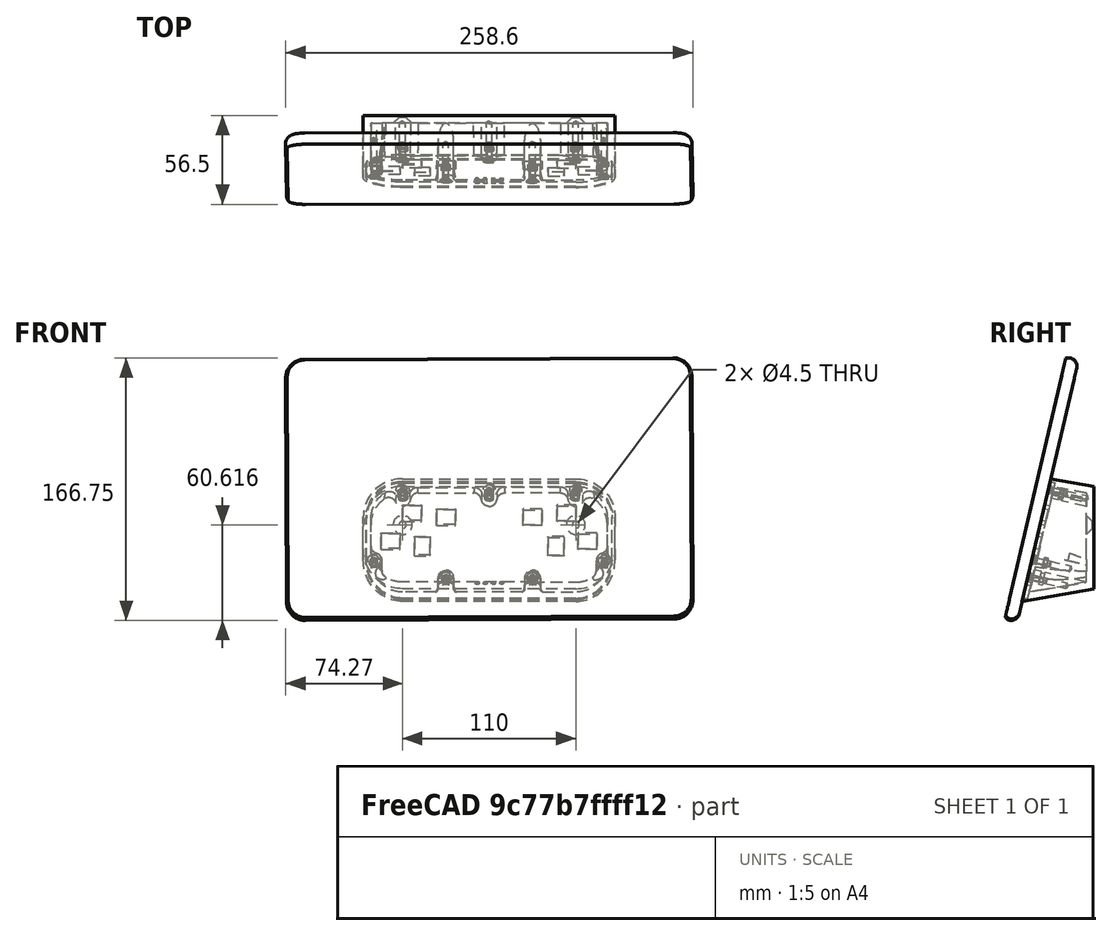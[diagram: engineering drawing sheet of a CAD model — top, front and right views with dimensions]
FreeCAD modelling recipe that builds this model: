
FCSTD DOCUMENT  (FreeCAD 0.21R33668 +7 (Git))
Label: assembly
License: All rights reserved
LicenseURL: http://en.wikipedia.org/wiki/All_rights_reserved
objects: Part::FeaturePython×9, App::GeometryPython×2
note: 9 computed .brp shape members not serialized (recipe doc carries the construction recipe); baked Part::Feature solids carry a one-line shape summary decoded from their .brp

FEATURE [Part::FeaturePython] b_wall_mount_001_  label="wall-mount_001"  # a2plus imported part (geometry in sourceFile) (typed FeaturePython)
  a2p_Version = 0.4.60n
  fixedPosition = true
  objectType = a2pPart
  sourceFile = ./wall-mount.FCStd
  subassemblyImport = false
  timeLastImport = 1.6917e+09
  updateColors = true
FEATURE [Part::FeaturePython] b_pixel_tablet_001_  label="pixel-tablet_001"  # a2plus imported part (geometry in sourceFile) (typed FeaturePython)
  Placement = pos=(0.0336065,-37.299,60.3169) rot=(-0.227279,-0.004053,0.000467;0.229357rad)
  a2p_Version = 0.4.60n
  fixedPosition = false
  objectType = a2pPart
  sourceFile = ./pixel-tablet.FCStd
  subassemblyImport = false
  timeLastImport = 1.69169e+09
  updateColors = true
FEATURE [Part::FeaturePython] Screw  label="M3x12-Screw"  # Fasteners workbench fastener (typed FeaturePython)
  Placement = pos=(-27.5,-42.008,4.07) rot=(1,0,0;1.34148rad)
  baseObject = -> b_wall_mount_001_ [Edge443]
  diameter = 3
  invert = true
  leftHanded = false
  length = 2
  lengthCustom = 12
  matchOuter = false
  offset = 0
  thread = false
  type = 31
FEATURE [Part::FeaturePython] Screw001  label="M3x12-Screw001"  # Fasteners workbench fastener (typed FeaturePython)
  Placement = pos=(27.5,-42.008,4.07) rot=(1,0,0;1.34148rad)
  baseObject = -> b_wall_mount_001_ [Edge451]
  diameter = 3
  invert = false
  leftHanded = false
  length = 2
  lengthCustom = 12
  matchOuter = false
  offset = 0
  thread = false
  type = 31
FEATURE [Part::FeaturePython] Screw002  label="M3x12-Screw002"  # Fasteners workbench fastener (typed FeaturePython)
  Placement = pos=(73,-39.5059,14.7889) rot=(1,0,0;1.34148rad)
  baseObject = -> b_wall_mount_001_ [Edge452]
  diameter = 3
  invert = false
  leftHanded = false
  length = 2
  lengthCustom = 12
  matchOuter = false
  offset = 0
  thread = false
  type = 31
FEATURE [Part::FeaturePython] Screw003  label="M3x12-Screw003"  # Fasteners workbench fastener (typed FeaturePython)
  Placement = pos=(55,-29.0937,59.3952) rot=(1,0,0;1.34148rad)
  baseObject = -> b_wall_mount_001_ [Edge453]
  diameter = 3
  invert = false
  leftHanded = false
  length = 2
  lengthCustom = 12
  matchOuter = false
  offset = 0
  thread = false
  type = 31
FEATURE [Part::FeaturePython] Screw004  label="M3x12-Screw004"  # Fasteners workbench fastener (typed FeaturePython)
  Placement = pos=(-2.2e-14,-29.0937,59.3952) rot=(1,0,0;1.34148rad)
  baseObject = -> b_wall_mount_001_ [Edge448]
  diameter = 3
  invert = false
  leftHanded = false
  length = 2
  lengthCustom = 12
  matchOuter = false
  offset = 0
  thread = false
  type = 31
FEATURE [Part::FeaturePython] Screw005  label="M3x12-Screw005"  # Fasteners workbench fastener (typed FeaturePython)
  Placement = pos=(-55,-29.0937,59.3952) rot=(1,0,0;1.34148rad)
  baseObject = -> b_wall_mount_001_ [Edge446]
  diameter = 3
  invert = true
  leftHanded = false
  length = 2
  lengthCustom = 12
  matchOuter = false
  offset = 0
  thread = false
  type = 31
FEATURE [Part::FeaturePython] Screw006  label="M3x12-Screw006"  # Fasteners workbench fastener (typed FeaturePython)
  Placement = pos=(-73,-39.5059,14.7889) rot=(1,0,0;1.34148rad)
  baseObject = -> b_wall_mount_001_ [Edge442]
  diameter = 3
  invert = true
  leftHanded = false
  length = 2
  lengthCustom = 12
  matchOuter = false
  offset = 0
  thread = false
  type = 31
FEATURE [App::GeometryPython] Camera  # WARN: FeaturePython — macro-defined, semantics opaque (R4)
  AspectRatio = 1
  FarDistance = 488.142
  FocalDistance = 334.778
  Height = 334.778
  HeightAngle = 60
  NearDistance = 228.782
  Placement = pos=(358.366,14.1692,42.0177) rot=(0.577346,0.577358,0.577346;2.09438rad)
  Projection = 1
  ViewportMapping = 3
FEATURE [App::GeometryPython] PointLight  # WARN: FeaturePython — macro-defined, semantics opaque (R4)
  Location = (548.5,-207.2,191.5)
  Placement = pos=(548.5,-207.2,191.5) rot=(0,0,1;0rad)
  Power = 60
  Radius = 2
